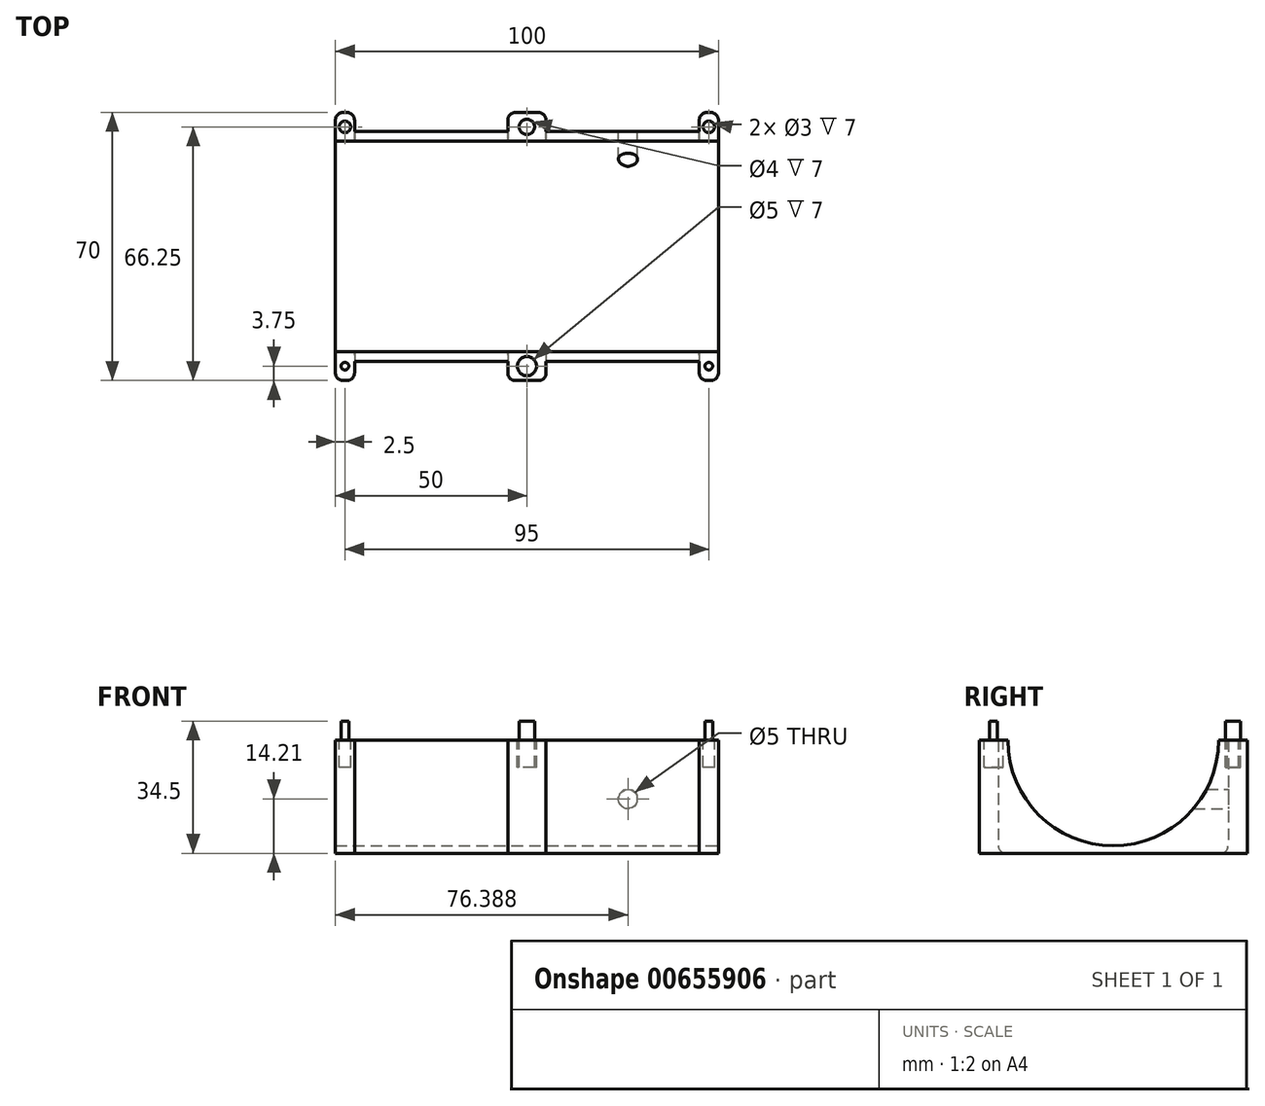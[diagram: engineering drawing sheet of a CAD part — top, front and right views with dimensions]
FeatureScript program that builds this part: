
annotation { "Feature Type Name" : "Feature", "Feature Type Description" : "" }
export const myFeature = defineFeature(function(context is Context, id is Id, definition is map)
    precondition{}
    {
        {
            var Q0;
            Q0=qCreatedBy(makeId("Top.planeOp"),FACE);
            var sketch = newSketch(context, id + "F0", { "sketchPlane" : qUnion([Q0])});
            skLineSegment(sketch, "E0.bottom", {"start": v(50, -30) * mm, "end": v(-50, -30) * mm});
            skLineSegment(sketch, "E0.top", {"start": v(50, 30) * mm, "end": v(-50, 30) * mm});
            skLineSegment(sketch, "E0.left", {"start": v(50, -30) * mm, "end": v(50, 30) * mm});
            skLineSegment(sketch, "E0.right", {"start": v(-50, -30) * mm, "end": v(-50, 30) * mm});
            skPoint(sketch, "E0.middle", {"position": v(0, 0) * mm});
            skLineSegment(sketch, "E1", {"start": v(-50, -30) * mm, "end": v(-50, -35) * mm});
            skLineSegment(sketch, "E2", {"start": v(-50, -35) * mm, "end": v(50, -35) * mm});
            skLineSegment(sketch, "E3", {"start": v(50, -35) * mm, "end": v(50, -30) * mm});
            skLineSegment(sketch, "E4", {"start": v(-45, -32.5) * mm, "end": v(-5, -32.5) * mm});
            skPoint(sketch, "E5.endSnap0", {"position": v(-25, -32.5) * mm});
            skLineSegment(sketch, "E6", {"start": v(5, -32.5) * mm, "end": v(45, -32.5) * mm});
            skLineSegment(sketch, "E7", {"start": v(-50, 30) * mm, "end": v(-50, 35) * mm});
            skLineSegment(sketch, "E8", {"start": v(-50, 35) * mm, "end": v(50, 35) * mm});
            skLineSegment(sketch, "E9", {"start": v(50, 35) * mm, "end": v(50, 30) * mm});
            skLineSegment(sketch, "E10", {"start": v(-45, -35) * mm, "end": v(-45, 35) * mm});
            skLineSegment(sketch, "E11", {"start": v(-5, -35) * mm, "end": v(-5, 35) * mm});
            skLineSegment(sketch, "E12", {"start": v(5, -35) * mm, "end": v(5, 35) * mm});
            skLineSegment(sketch, "E13", {"start": v(45, -35) * mm, "end": v(45, 35) * mm});
            skSolve(sketch);
        }
        {
            var Q0;
            {var subQ0=sQuery(id+"F0.wireOp",EDGE,"E9");Q0=makeQuery(id+"F0.imprint","IMPRINT",FACE,{"disambiguationData":[TD([[makeQuery(id+"F0.imprint","IMPRINT",EDGE,{"derivedFrom":subQ0}),-1.0]])]});}
            var Q1;
            {var subQ0=sQuery(id+"F0.wireOp",EDGE,"E7");Q1=makeQuery(id+"F0.imprint","IMPRINT",FACE,{"disambiguationData":[TD([[makeQuery(id+"F0.imprint","IMPRINT",EDGE,{"derivedFrom":subQ0}),-1.0]])]});}
            var Q2;
            {var subQ0=sQuery(id+"F0.wireOp",EDGE,"E0.left");Q2=makeQuery(id+"F0.imprint","IMPRINT",FACE,{"disambiguationData":[TD([[makeQuery(id+"F0.imprint","IMPRINT",EDGE,{"derivedFrom":subQ0}),1.0]])]});}
            var Q3;
            {var subQ0=sQuery(id+"F0.wireOp",EDGE,"E3");Q3=makeQuery(id+"F0.imprint","IMPRINT",FACE,{"disambiguationData":[TD([[makeQuery(id+"F0.imprint","IMPRINT",EDGE,{"derivedFrom":subQ0}),1.0]])]});}
            var Q4;
            {var subQ0=sQuery(id+"F0.wireOp",EDGE,"E0.right");Q4=makeQuery(id+"F0.imprint","IMPRINT",FACE,{"disambiguationData":[TD([[makeQuery(id+"F0.imprint","IMPRINT",EDGE,{"derivedFrom":subQ0}),-1.0]])]});}
            var Q5;
            {var subQ0=sQuery(id+"F0.wireOp",EDGE,"E12");var subQ1=sQuery(id+"F0.wireOp",EDGE,"E0.top");var subQ2=makeQuery(id+"F0.imprint","INTERSECT",VERTEX,{"derivedFrom":[subQ1,subQ0]});Q5=makeQuery(id+"F0.imprint","IMPRINT",FACE,{"disambiguationData":[TD([[makeQuery(id+"F0.imprint","IMPRINT",EDGE,{"disambiguationData":[TD([[subQ2,-1.0]])],"derivedFrom":subQ1}),-1.0]])]});}
            var Q6;
            {var subQ2=sQuery(id+"F0.wireOp",EDGE,"E0.bottom");var subQ6=sQuery(id+"F0.wireOp",EDGE,"E12");var subQ9=makeQuery(id+"F0.imprint","INTERSECT",VERTEX,{"derivedFrom":[subQ2,subQ6]});Q6=makeQuery(id+"F0.imprint","IMPRINT",FACE,{"disambiguationData":[TD([[makeQuery(id+"F0.imprint","IMPRINT",EDGE,{"disambiguationData":[TD([[subQ9,-1.0]])],"derivedFrom":subQ2}),1.0]])]});}
            var Q7;
            {var subQ0=sQuery(id+"F0.wireOp",EDGE,"E13");var subQ1=sQuery(id+"F0.wireOp",EDGE,"E0.bottom");var subQ2=makeQuery(id+"F0.imprint","INTERSECT",VERTEX,{"derivedFrom":[subQ1,subQ0]});Q7=makeQuery(id+"F0.imprint","IMPRINT",FACE,{"disambiguationData":[TD([[makeQuery(id+"F0.imprint","IMPRINT",EDGE,{"disambiguationData":[TD([[subQ2,-1.0]])],"derivedFrom":subQ1}),-1.0]])]});}
            var Q8;
            {var subQ0=sQuery(id+"F0.wireOp",EDGE,"E11");var subQ1=sQuery(id+"F0.wireOp",EDGE,"E0.bottom");var subQ2=makeQuery(id+"F0.imprint","INTERSECT",VERTEX,{"derivedFrom":[subQ1,subQ0]});Q8=makeQuery(id+"F0.imprint","IMPRINT",FACE,{"disambiguationData":[TD([[makeQuery(id+"F0.imprint","IMPRINT",EDGE,{"disambiguationData":[TD([[subQ2,-1.0]])],"derivedFrom":subQ1}),-1.0]])]});}
            var Q9;
            {var subQ0=sQuery(id+"F0.wireOp",EDGE,"E12");var subQ1=sQuery(id+"F0.wireOp",EDGE,"E0.bottom");var subQ2=makeQuery(id+"F0.imprint","INTERSECT",VERTEX,{"derivedFrom":[subQ1,subQ0]});Q9=makeQuery(id+"F0.imprint","IMPRINT",FACE,{"disambiguationData":[TD([[makeQuery(id+"F0.imprint","IMPRINT",EDGE,{"disambiguationData":[TD([[subQ2,-1.0]])],"derivedFrom":subQ1}),-1.0]])]});}
            var Q10;
            {var subQ4=sQuery(id+"F0.wireOp",EDGE,"E1");Q10=makeQuery(id+"F0.imprint","IMPRINT",FACE,{"disambiguationData":[TD([[makeQuery(id+"F0.imprint","IMPRINT",EDGE,{"derivedFrom":subQ4}),1.0]])]});}
            extrude(context, id + "F1", {"entities" : qUnion([Q0, Q1, Q2, Q3, Q4, Q5, Q6, Q7, Q8, Q9, Q10]), "depth" : 29.5 * mm, "offsetDistance" : 25 * mm});
        }
        {
            var Q0;
            Q0=makeQuery(id+"F1.opExtrude","SWEPT_FACE",FACE,{"disambiguationData":[OSD([sQuery(id+"F0.wireOp",EDGE,"E0.left")])]});
            var sketch = newSketch(context, id + "F2", { "sketchPlane" : qUnion([Q0])});
            skLineSegment(sketch, "E14", {"start": v(-30, 2) * mm, "end": v(30, 2) * mm});
            skLineSegment(sketch, "E15", {"start": v(0, 2) * mm, "end": v(0, 29.5) * mm});
            skCircle(sketch, "E16", {"center": v(0, 29.5) * mm, "radius": 27.5 * mm});
            skSolve(sketch);
        }
        {
            var Q0;
            {var subQ0=sQuery(id+"F2.wireOp",EDGE,"E15");Q0=makeQuery(id+"F2.imprint","IMPRINT",FACE,{"disambiguationData":[TD([[makeQuery(id+"F2.imprint","IMPRINT",EDGE,{"derivedFrom":subQ0}),1.0]])]});}
            var Q1;
            {var subQ0=sQuery(id+"F2.wireOp",EDGE,"E15");Q1=makeQuery(id+"F2.imprint","IMPRINT",FACE,{"disambiguationData":[TD([[makeQuery(id+"F2.imprint","IMPRINT",EDGE,{"derivedFrom":subQ0}),-1.0]])]});}
            extrude(context, id + "F3", {"entities" : qUnion([Q0, Q1]), "operationType" : NewBodyOperationType.REMOVE, "endBound" : BoundingType.THROUGH_ALL, "oppositeDirection" : true, "depth" : 25 * mm, "offsetDistance" : 25 * mm});
        }
        {
            var Q0;
            {var subQ0=sQuery(id+"F0.wireOp",EDGE,"E11");var subQ3=sQuery(id+"F0.wireOp",EDGE,"E0.bottom");var subQ5=sQuery(id+"F0.wireOp",EDGE,"E2");var subQ7=sQuery(id+"F0.wireOp",EDGE,"E3");var subQ8=sQuery(id+"F0.wireOp",EDGE,"E13");var subQ10=sQuery(id+"F0.wireOp",EDGE,"E12");var subQ12=sQuery(id+"F0.wireOp",EDGE,"E1");var subQ13=sQuery(id+"F0.wireOp",EDGE,"E10");var subQ15=makeQuery(id+"F0.imprint","INTERSECT",VERTEX,{"derivedFrom":[subQ3,subQ8]});var subQ19=sQuery(id+"F0.wireOp",EDGE,"E9");var subQ20=sQuery(id+"F0.wireOp",EDGE,"E0.left");var subQ23=sQuery(id+"F0.wireOp",EDGE,"E7");var subQ24=sQuery(id+"F0.wireOp",EDGE,"E0.right");Q0=makeQuery(id+"F3.boolean.opBoolean","SPLIT",FACE,{"disambiguationData":[TD([makeQuery(id+"F1.opExtrude","SWEPT_FACE",FACE,{"disambiguationData":[OSD([subQ3]),TDD([makeQuery(id+"F0.imprint","IMPRINT",EDGE,{"disambiguationData":[TD([[subQ15,-1.0]])],"derivedFrom":subQ3})])]})])],"derivedFrom":makeQuery(id+"F1.opExtrude","CAP_FACE",FACE,{"disambiguationData":[OSD([subQ3,sQuery(id+"F0.wireOp",EDGE,"E0.top"),subQ20,subQ24,subQ12,subQ5,subQ7,subQ23,sQuery(id+"F0.wireOp",EDGE,"E8"),subQ19,subQ13,subQ0,subQ10,subQ8])],"isStart":false})});}
            var sketch = newSketch(context, id + "F4", { "sketchPlane" : qUnion([Q0])});
            skCircle(sketch, "E17", {"center": v(47.5, -31.25) * mm, "radius": 1 * mm});
            skCircle(sketch, "E18", {"center": v(0, -31.25) * mm, "radius": 2.5 * mm});
            skCircle(sketch, "E19", {"center": v(-47.5, -31.25) * mm, "radius": 1 * mm});
            skSolve(sketch);
        }
        {
            var Q0;
            {var subQ0=sQuery(id+"F0.wireOp",EDGE,"E12");var subQ1=sQuery(id+"F0.wireOp",EDGE,"E8");var subQ3=sQuery(id+"F0.wireOp",EDGE,"E0.top");var subQ5=sQuery(id+"F0.wireOp",EDGE,"E9");var subQ6=sQuery(id+"F0.wireOp",EDGE,"E13");var subQ8=sQuery(id+"F0.wireOp",EDGE,"E11");var subQ10=sQuery(id+"F0.wireOp",EDGE,"E7");var subQ11=sQuery(id+"F0.wireOp",EDGE,"E10");var subQ14=makeQuery(id+"F0.imprint","INTERSECT",VERTEX,{"derivedFrom":[subQ3,subQ6]});var subQ16=sQuery(id+"F0.wireOp",EDGE,"E3");var subQ17=sQuery(id+"F0.wireOp",EDGE,"E0.left");var subQ18=sQuery(id+"F0.wireOp",EDGE,"E1");var subQ19=sQuery(id+"F0.wireOp",EDGE,"E0.right");Q0=makeQuery(id+"F3.boolean.opBoolean","SPLIT",FACE,{"disambiguationData":[TD([makeQuery(id+"F1.opExtrude","SWEPT_FACE",FACE,{"disambiguationData":[OSD([subQ3]),TDD([makeQuery(id+"F0.imprint","IMPRINT",EDGE,{"disambiguationData":[TD([[subQ14,-1.0]])],"derivedFrom":subQ3})])]})])],"derivedFrom":makeQuery(id+"F1.opExtrude","CAP_FACE",FACE,{"disambiguationData":[OSD([sQuery(id+"F0.wireOp",EDGE,"E0.bottom"),subQ3,subQ17,subQ19,subQ18,sQuery(id+"F0.wireOp",EDGE,"E2"),subQ16,subQ10,subQ1,subQ5,subQ11,subQ8,subQ0,subQ6])],"isStart":false})});}
            var sketch = newSketch(context, id + "F5", { "sketchPlane" : qUnion([Q0])});
            skPoint(sketch, "E20.startSnap0", {"position": v(-45, 32.5) * mm});
            skCircle(sketch, "E21", {"center": v(-47.5, 31.25) * mm, "radius": 1.5 * mm});
            skCircle(sketch, "E22", {"center": v(0, 31.25) * mm, "radius": 2 * mm});
            skCircle(sketch, "E23", {"center": v(47.5, 31.25) * mm, "radius": 1.5 * mm});
            skSolve(sketch);
        }
        {
            var Q0;
            Q0=makeQuery(id+"F4.imprint","IMPRINT",FACE,{"disambiguationData":[TD([[makeQuery(id+"F4.imprint","IMPRINT",EDGE,{"derivedFrom":sQuery(id+"F4.wireOp",EDGE,"E19")}),1.0]])]});
            var Q1;
            Q1=makeQuery(id+"F4.imprint","IMPRINT",FACE,{"disambiguationData":[TD([[makeQuery(id+"F4.imprint","IMPRINT",EDGE,{"derivedFrom":sQuery(id+"F4.wireOp",EDGE,"E17")}),1.0]])]});
            var Q2;
            Q2=makeQuery(id+"F5.imprint","IMPRINT",FACE,{"disambiguationData":[TD([[makeQuery(id+"F5.imprint","IMPRINT",EDGE,{"derivedFrom":sQuery(id+"F5.wireOp",EDGE,"E22")}),1.0]])]});
            extrude(context, id + "F6", {"entities" : qUnion([Q0, Q1, Q2]), "operationType" : NewBodyOperationType.ADD, "depth" : 5 * mm, "offsetDistance" : 25 * mm});
        }
        {
            var Q0;
            Q0=makeQuery(id+"F4.imprint","IMPRINT",FACE,{"disambiguationData":[TD([[makeQuery(id+"F4.imprint","IMPRINT",EDGE,{"derivedFrom":sQuery(id+"F4.wireOp",EDGE,"E18")}),1.0]])]});
            var Q1;
            Q1 = qSketchRegion(id + "F5", true);
            extrude(context, id + "F7", {"entities" : qUnion([Q0, Q1]), "operationType" : NewBodyOperationType.REMOVE, "oppositeDirection" : true, "depth" : 7 * mm, "offsetDistance" : 25 * mm});
        }
        {
            var Q0;
            {var subQ0=sQuery(id+"F0.wireOp",EDGE,"E0.top");Q0=makeQuery(id+"F1.opExtrude","SWEPT_FACE",FACE,{"disambiguationData":[OSD([subQ0]),TDD([makeQuery(id+"F0.imprint","IMPRINT",EDGE,{"disambiguationData":[TD([[makeQuery(id+"F0.imprint","INTERSECT",VERTEX,{"derivedFrom":[subQ0,sQuery(id+"F0.wireOp",EDGE,"E13")]}),-1.0]])],"derivedFrom":subQ0})])]});}
            var sketch = newSketch(context, id + "F8", { "sketchPlane" : qUnion([Q0])});
            skCircle(sketch, "E24", {"center": v(-26.39, 14.21) * mm, "radius": 2.5 * mm});
            skSolve(sketch);
        }
        {
            var Q0;
            Q0=makeQuery(id+"F8.imprint","IMPRINT",FACE,{"disambiguationData":[TD([[makeQuery(id+"F8.imprint","IMPRINT",EDGE,{"derivedFrom":sQuery(id+"F8.wireOp",EDGE,"E24")}),1.0]])]});
            extrude(context, id + "F9", {"entities" : qUnion([Q0]), "operationType" : NewBodyOperationType.REMOVE, "oppositeDirection" : true, "depth" : 10 * mm, "offsetDistance" : 25 * mm});
        }
        {
            var Q0;
            Q0=makeQuery(id+"F1.opExtrude","SWEPT_EDGE",EDGE,{"disambiguationData":[OSD([sQuery(id+"F0.wireOp",EDGE,"E2"),sQuery(id+"F0.wireOp",EDGE,"E3")])]});
            var Q1;
            Q1=makeQuery(id+"F1.opExtrude","SWEPT_EDGE",EDGE,{"disambiguationData":[OSD([sQuery(id+"F0.wireOp",EDGE,"E2"),sQuery(id+"F0.wireOp",EDGE,"E13")])]});
            var Q2;
            Q2=makeQuery(id+"F1.opExtrude","SWEPT_EDGE",EDGE,{"disambiguationData":[OSD([sQuery(id+"F0.wireOp",EDGE,"E2"),sQuery(id+"F0.wireOp",EDGE,"E12")])]});
            var Q3;
            Q3=makeQuery(id+"F1.opExtrude","SWEPT_EDGE",EDGE,{"disambiguationData":[OSD([sQuery(id+"F0.wireOp",EDGE,"E2"),sQuery(id+"F0.wireOp",EDGE,"E11")])]});
            var Q4;
            Q4=makeQuery(id+"F1.opExtrude","SWEPT_EDGE",EDGE,{"disambiguationData":[OSD([sQuery(id+"F0.wireOp",EDGE,"E2"),sQuery(id+"F0.wireOp",EDGE,"E10")])]});
            var Q5;
            Q5=makeQuery(id+"F1.opExtrude","SWEPT_EDGE",EDGE,{"disambiguationData":[OSD([sQuery(id+"F0.wireOp",EDGE,"E1"),sQuery(id+"F0.wireOp",EDGE,"E2")])]});
            var Q6;
            Q6=makeQuery(id+"F1.opExtrude","SWEPT_EDGE",EDGE,{"disambiguationData":[OSD([sQuery(id+"F0.wireOp",EDGE,"E8"),sQuery(id+"F0.wireOp",EDGE,"E13")])]});
            var Q7;
            Q7=makeQuery(id+"F1.opExtrude","SWEPT_EDGE",EDGE,{"disambiguationData":[OSD([sQuery(id+"F0.wireOp",EDGE,"E8"),sQuery(id+"F0.wireOp",EDGE,"E9")])]});
            var Q8;
            Q8=makeQuery(id+"F1.opExtrude","SWEPT_EDGE",EDGE,{"disambiguationData":[OSD([sQuery(id+"F0.wireOp",EDGE,"E8"),sQuery(id+"F0.wireOp",EDGE,"E12")])]});
            var Q9;
            Q9=makeQuery(id+"F1.opExtrude","SWEPT_EDGE",EDGE,{"disambiguationData":[OSD([sQuery(id+"F0.wireOp",EDGE,"E8"),sQuery(id+"F0.wireOp",EDGE,"E11")])]});
            var Q10;
            Q10=makeQuery(id+"F1.opExtrude","SWEPT_EDGE",EDGE,{"disambiguationData":[OSD([sQuery(id+"F0.wireOp",EDGE,"E8"),sQuery(id+"F0.wireOp",EDGE,"E10")])]});
            var Q11;
            Q11=makeQuery(id+"F1.opExtrude","SWEPT_EDGE",EDGE,{"disambiguationData":[OSD([sQuery(id+"F0.wireOp",EDGE,"E7"),sQuery(id+"F0.wireOp",EDGE,"E8")])]});
            fillet(context, id + "F10", {"entities" : qUnion([Q0, Q1, Q2, Q3, Q4, Q5, Q6, Q7, Q8, Q9, Q10, Q11]), "radius" : 2 * mm, "tangentPropagation" : true, "allowEdgeOverflow" : false});
        }
        {
            var Q0;
            {var subQ0=sQuery(id+"F0.wireOp",EDGE,"E0.top");Q0=makeQuery(id+"F1.opExtrude","CAP_EDGE",EDGE,{"disambiguationData":[OSD([subQ0]),TDD([makeQuery(id+"F0.imprint","IMPRINT",EDGE,{"disambiguationData":[TD([[makeQuery(id+"F0.imprint","INTERSECT",VERTEX,{"derivedFrom":[subQ0,sQuery(id+"F0.wireOp",EDGE,"E13")]}),-1.0]])],"derivedFrom":subQ0})])],"isStart":true});}
            var Q1;
            {var subQ0=sQuery(id+"F0.wireOp",EDGE,"E0.top");Q1=makeQuery(id+"F1.opExtrude","CAP_EDGE",EDGE,{"disambiguationData":[OSD([subQ0]),TDD([makeQuery(id+"F0.imprint","IMPRINT",EDGE,{"disambiguationData":[TD([[makeQuery(id+"F0.imprint","INTERSECT",VERTEX,{"derivedFrom":[subQ0,sQuery(id+"F0.wireOp",EDGE,"E11")]}),-1.0]])],"derivedFrom":subQ0})])],"isStart":true});}
            var Q2;
            {var subQ0=sQuery(id+"F0.wireOp",EDGE,"E0.bottom");Q2=makeQuery(id+"F1.opExtrude","CAP_EDGE",EDGE,{"disambiguationData":[OSD([subQ0]),TDD([makeQuery(id+"F0.imprint","IMPRINT",EDGE,{"disambiguationData":[TD([[makeQuery(id+"F0.imprint","INTERSECT",VERTEX,{"derivedFrom":[subQ0,sQuery(id+"F0.wireOp",EDGE,"E11")]}),-1.0]])],"derivedFrom":subQ0})])],"isStart":true});}
            var Q3;
            {var subQ0=sQuery(id+"F0.wireOp",EDGE,"E0.bottom");Q3=makeQuery(id+"F1.opExtrude","CAP_EDGE",EDGE,{"disambiguationData":[OSD([subQ0]),TDD([makeQuery(id+"F0.imprint","IMPRINT",EDGE,{"disambiguationData":[TD([[makeQuery(id+"F0.imprint","INTERSECT",VERTEX,{"derivedFrom":[subQ0,sQuery(id+"F0.wireOp",EDGE,"E13")]}),-1.0]])],"derivedFrom":subQ0})])],"isStart":true});}
            fillet(context, id + "F11", {"entities" : qUnion([Q0, Q1, Q2, Q3]), "radius" : 2 * mm, "tangentPropagation" : true, "allowEdgeOverflow" : false});
        }
    });
